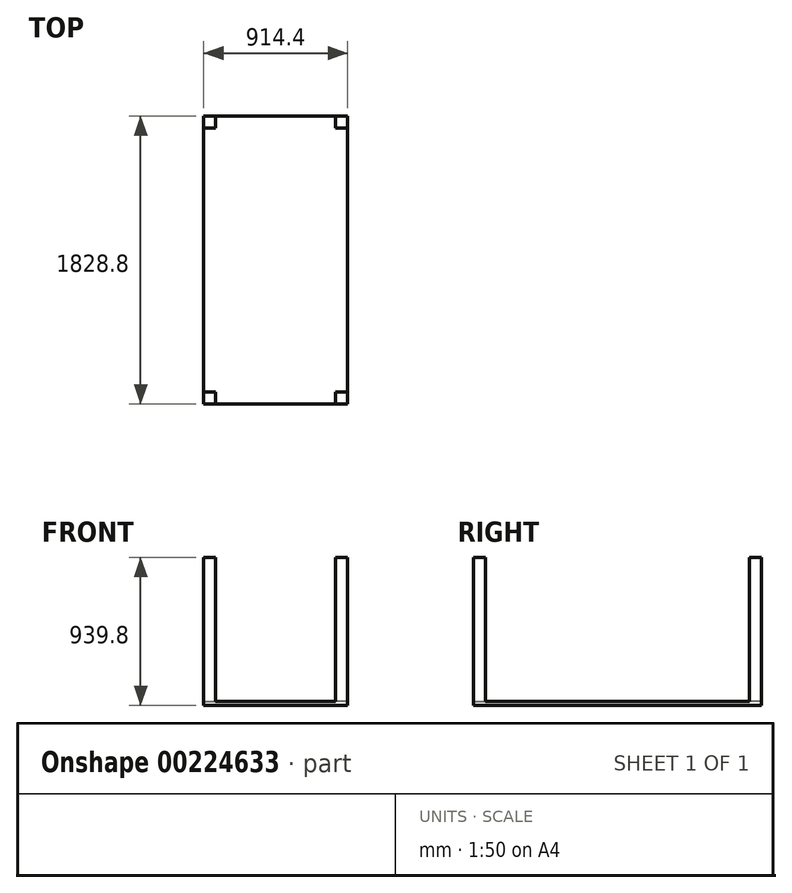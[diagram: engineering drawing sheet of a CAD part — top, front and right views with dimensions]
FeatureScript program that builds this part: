
annotation { "Feature Type Name" : "Feature", "Feature Type Description" : "" }
export const myFeature = defineFeature(function(context is Context, id is Id, definition is map)
    precondition{}
    {
        {
            var Q0;
            Q0=qCreatedBy(makeId("Top.planeOp"),FACE);
            var sketch = newSketch(context, id + "F0", { "sketchPlane" : qUnion([Q0])});
            skLineSegment(sketch, "E0.bottom", {"start": v(457.2, -914.4) * mm, "end": v(-457.2, -914.4) * mm});
            skLineSegment(sketch, "E0.top", {"start": v(457.2, 914.4) * mm, "end": v(-457.2, 914.4) * mm});
            skLineSegment(sketch, "E0.left", {"start": v(457.2, -914.4) * mm, "end": v(457.2, 914.4) * mm});
            skLineSegment(sketch, "E0.right", {"start": v(-457.2, -914.4) * mm, "end": v(-457.2, 914.4) * mm});
            skPoint(sketch, "E0.middle", {"position": v(0, 0) * mm});
            skSolve(sketch);
        }
        {
            var Q0;
            Q0=makeQuery(id+"F0.imprint","IMPRINT",FACE,{"disambiguationData":[TD([[makeQuery(id+"F0.imprint","IMPRINT",EDGE,{"derivedFrom":sQuery(id+"F0.wireOp",EDGE,"E0.bottom")}),-1.0]])]});
            extrude(context, id + "F1", {"entities" : qUnion([Q0]), "depth" : 25.4 * mm});
        }
        {
            var Q0;
            Q0=makeQuery(id+"F1.opExtrude","CAP_FACE",FACE,{"disambiguationData":[OSD([sQuery(id+"F0.wireOp",EDGE,"E0.bottom"),sQuery(id+"F0.wireOp",EDGE,"E0.top"),sQuery(id+"F0.wireOp",EDGE,"E0.left"),sQuery(id+"F0.wireOp",EDGE,"E0.right")])],"isStart":false});
            var sketch = newSketch(context, id + "F2", { "sketchPlane" : qUnion([Q0])});
            skLineSegment(sketch, "E1.bottom", {"start": v(-457.2, 914.4) * mm, "end": v(-381, 914.4) * mm});
            skLineSegment(sketch, "E1.top", {"start": v(-457.2, 838.2) * mm, "end": v(-381, 838.2) * mm});
            skLineSegment(sketch, "E1.left", {"start": v(-457.2, 914.4) * mm, "end": v(-457.2, 838.2) * mm});
            skLineSegment(sketch, "E1.right", {"start": v(-381, 914.4) * mm, "end": v(-381, 838.2) * mm});
            skLineSegment(sketch, "E2.bottom", {"start": v(457.2, 914.4) * mm, "end": v(381, 914.4) * mm});
            skLineSegment(sketch, "E2.top", {"start": v(457.2, 838.2) * mm, "end": v(381, 838.2) * mm});
            skLineSegment(sketch, "E2.left", {"start": v(457.2, 914.4) * mm, "end": v(457.2, 838.2) * mm});
            skLineSegment(sketch, "E2.right", {"start": v(381, 914.4) * mm, "end": v(381, 838.2) * mm});
            skLineSegment(sketch, "E3.bottom", {"start": v(-457.2, -914.4) * mm, "end": v(-457.2, -914.4) * mm});
            skLineSegment(sketch, "E3.top", {"start": v(-457.2, -838.2) * mm, "end": v(-457.2, -838.2) * mm});
            skLineSegment(sketch, "E3.left", {"start": v(-457.2, -914.4) * mm, "end": v(-457.2, -838.2) * mm});
            skLineSegment(sketch, "E3.right", {"start": v(-457.2, -914.4) * mm, "end": v(-457.2, -838.2) * mm});
            skLineSegment(sketch, "E4.bottom", {"start": v(-457.2, -914.4) * mm, "end": v(-381, -914.4) * mm});
            skLineSegment(sketch, "E4.top", {"start": v(-457.2, -838.2) * mm, "end": v(-381, -838.2) * mm});
            skLineSegment(sketch, "E4.right", {"start": v(-381, -914.4) * mm, "end": v(-381, -838.2) * mm});
            skLineSegment(sketch, "E5.bottom", {"start": v(457.2, -914.4) * mm, "end": v(381, -914.4) * mm});
            skLineSegment(sketch, "E5.top", {"start": v(457.2, -838.2) * mm, "end": v(381, -838.2) * mm});
            skLineSegment(sketch, "E5.left", {"start": v(457.2, -914.4) * mm, "end": v(457.2, -838.2) * mm});
            skLineSegment(sketch, "E5.right", {"start": v(381, -914.4) * mm, "end": v(381, -838.2) * mm});
            skSolve(sketch);
        }
        {
            var Q0;
            Q0=makeQuery(id+"F2.imprint","IMPRINT",FACE,{"disambiguationData":[TD([[makeQuery(id+"F2.imprint","IMPRINT",EDGE,{"derivedFrom":sQuery(id+"F2.wireOp",EDGE,"E1.bottom")}),1.0]])]});
            var Q1;
            Q1=makeQuery(id+"F2.imprint","IMPRINT",FACE,{"disambiguationData":[TD([[makeQuery(id+"F2.imprint","IMPRINT",EDGE,{"derivedFrom":sQuery(id+"F2.wireOp",EDGE,"E2.bottom")}),1.0]])]});
            var Q2;
            Q2=makeQuery(id+"F2.imprint","IMPRINT",FACE,{"disambiguationData":[TD([[makeQuery(id+"F2.imprint","IMPRINT",EDGE,{"derivedFrom":sQuery(id+"F2.wireOp",EDGE,"E5.bottom")}),-1.0]])]});
            var Q3;
            Q3=makeQuery(id+"F2.imprint","IMPRINT",FACE,{"disambiguationData":[TD([[makeQuery(id+"F2.imprint","IMPRINT",EDGE,{"derivedFrom":sQuery(id+"F2.wireOp",EDGE,"E4.bottom")}),-1.0]])]});
            extrude(context, id + "F3", {"entities" : qUnion([Q0, Q1, Q2, Q3]), "operationType" : NewBodyOperationType.ADD, "depth" : 914.4 * mm});
        }
    });
